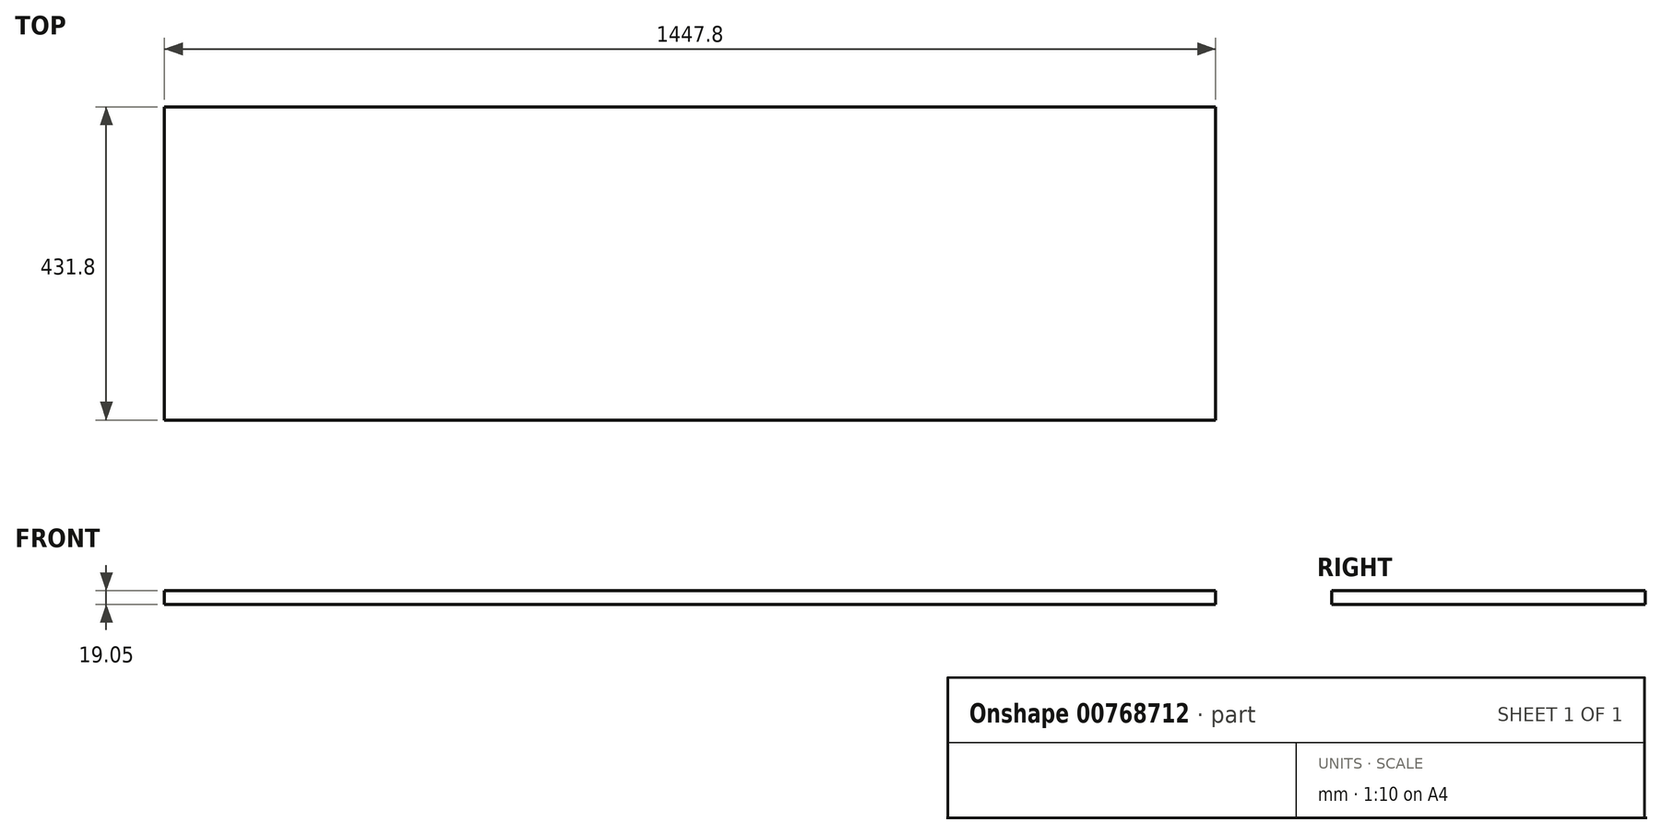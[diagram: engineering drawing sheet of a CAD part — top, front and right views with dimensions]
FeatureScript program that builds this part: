
annotation { "Feature Type Name" : "Feature", "Feature Type Description" : "" }
export const myFeature = defineFeature(function(context is Context, id is Id, definition is map)
    precondition{}
    {
        {
            var Q0;
            Q0=qCreatedBy(makeId("Top.planeOp"),FACE);
            var sketch = newSketch(context, id + "F0", { "sketchPlane" : qUnion([Q0])});
            skLineSegment(sketch, "E0.bottom", {"start": v(-723.9, 215.9) * mm, "end": v(723.9, 215.9) * mm});
            skLineSegment(sketch, "E0.top", {"start": v(-723.9, -215.9) * mm, "end": v(723.9, -215.9) * mm});
            skLineSegment(sketch, "E0.left", {"start": v(-723.9, 215.9) * mm, "end": v(-723.9, -215.9) * mm});
            skLineSegment(sketch, "E0.right", {"start": v(723.9, 215.9) * mm, "end": v(723.9, -215.9) * mm});
            skPoint(sketch, "E0.middle", {"position": v(0, 0) * mm});
            skSolve(sketch);
        }
        {
            var Q0;
            Q0=makeQuery(id+"F0.imprint","IMPRINT",FACE,{"disambiguationData":[TD([[makeQuery(id+"F0.imprint","IMPRINT",EDGE,{"derivedFrom":sQuery(id+"F0.wireOp",EDGE,"E0.bottom")}),-1.0]])]});
            extrude(context, id + "F1", {"entities" : qUnion([Q0]), "depth" : 19.05 * mm, "offsetDistance" : 25.4 * mm});
        }
    });
